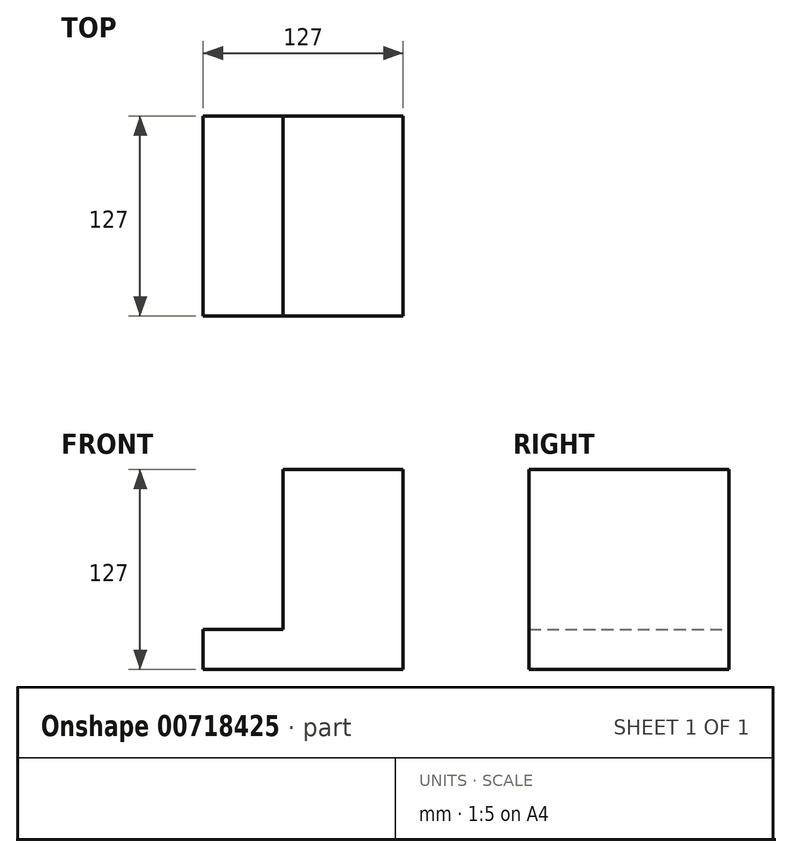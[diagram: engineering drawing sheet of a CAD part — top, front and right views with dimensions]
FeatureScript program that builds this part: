
annotation { "Feature Type Name" : "Feature", "Feature Type Description" : "" }
export const myFeature = defineFeature(function(context is Context, id is Id, definition is map)
    precondition{}
    {
        {
            var Q0;
            Q0=qCreatedBy(makeId("Front.planeOp"),FACE);
            var sketch = newSketch(context, id + "F0", { "sketchPlane" : qUnion([Q0])});
            skLineSegment(sketch, "E0", {"start": v(-70.66, -63.37) * mm, "end": v(56.34, -63.37) * mm});
            skLineSegment(sketch, "E1", {"start": v(56.34, -63.37) * mm, "end": v(56.34, 63.63) * mm});
            skLineSegment(sketch, "E2", {"start": v(56.34, 63.63) * mm, "end": v(-19.86, 63.63) * mm});
            skLineSegment(sketch, "E3", {"start": v(-19.86, 63.63) * mm, "end": v(-19.86, -37.97) * mm});
            skLineSegment(sketch, "E4", {"start": v(-19.86, -37.97) * mm, "end": v(-70.66, -37.97) * mm});
            skLineSegment(sketch, "E5", {"start": v(-70.66, -37.97) * mm, "end": v(-70.66, -63.37) * mm});
            skSolve(sketch);
        }
        {
            var Q0;
            Q0=makeQuery(id+"F0.imprint","IMPRINT",FACE,{"disambiguationData":[TD([[makeQuery(id+"F0.imprint","IMPRINT",EDGE,{"derivedFrom":sQuery(id+"F0.wireOp",EDGE,"E0")}),1.0]])]});
            extrude(context, id + "F1", {"entities" : qUnion([Q0]), "depth" : 127 * mm, "offsetDistance" : 25.4 * mm});
        }
    });
